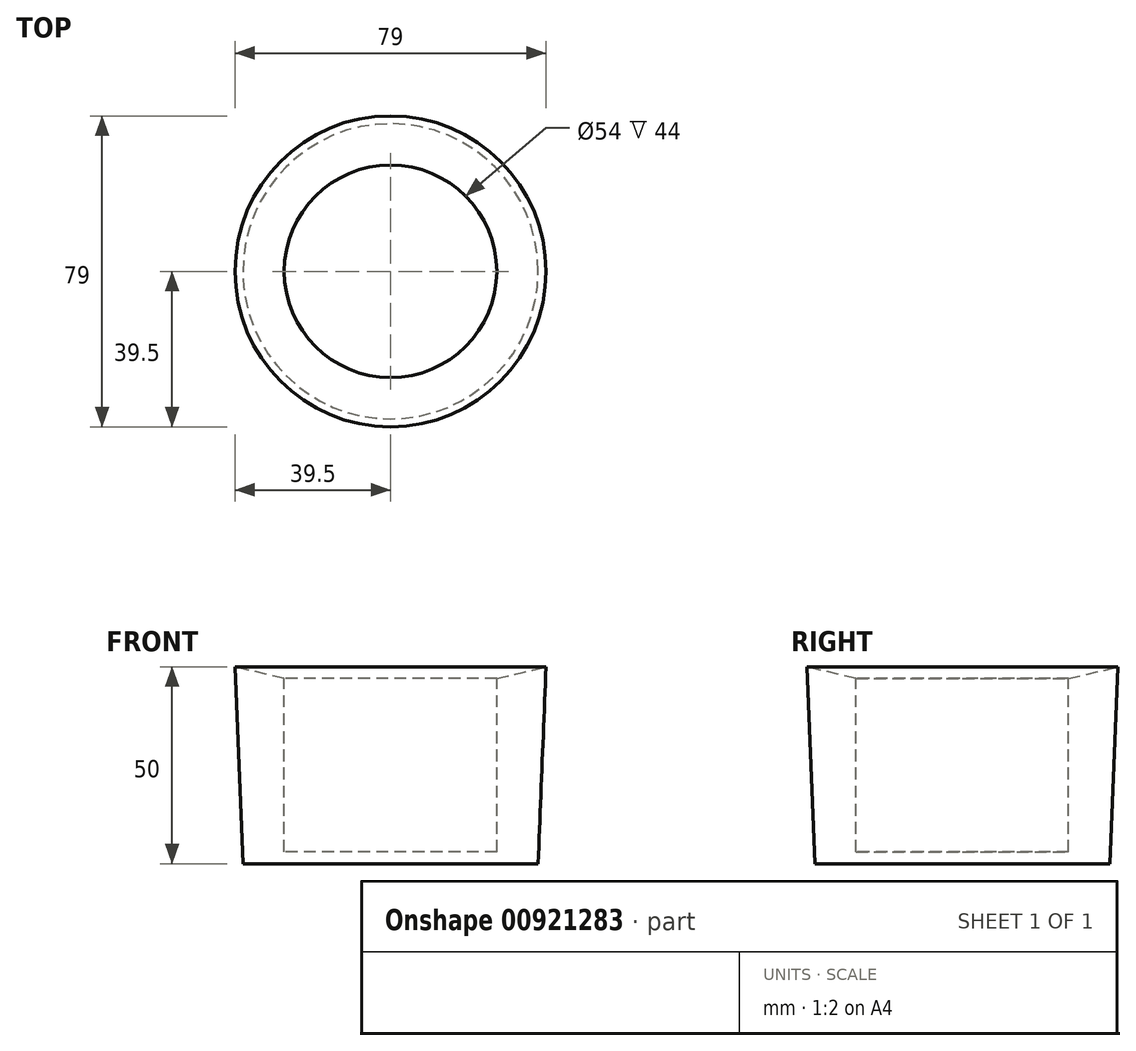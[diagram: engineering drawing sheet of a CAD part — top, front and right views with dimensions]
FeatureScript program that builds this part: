
annotation { "Feature Type Name" : "Feature", "Feature Type Description" : "" }
export const myFeature = defineFeature(function(context is Context, id is Id, definition is map)
    precondition{}
    {
        {
            var Q0;
            Q0=qCreatedBy(makeId("Front.planeOp"),FACE);
            var sketch = newSketch(context, id + "F0", { "sketchPlane" : qUnion([Q0])});
            skLineSegment(sketch, "E0", {"start": v(0, 0) * mm, "end": v(-37.5, 0) * mm});
            skLineSegment(sketch, "E1", {"start": v(-37.5, 0) * mm, "end": v(-39.5, 50) * mm});
            skLineSegment(sketch, "E2", {"start": v(-39.5, 50) * mm, "end": v(-27, 47) * mm});
            skLineSegment(sketch, "E3", {"start": v(-27, 47) * mm, "end": v(-27, 3) * mm});
            skLineSegment(sketch, "E4", {"start": v(-27, 3) * mm, "end": v(0, 3) * mm});
            skLineSegment(sketch, "E5", {"start": v(0, 3) * mm, "end": v(0, 0) * mm});
            skSolve(sketch);
        }
        {
            var Q0;
            Q0=makeQuery(id+"F0.imprint","IMPRINT",FACE,{"disambiguationData":[TD([[makeQuery(id+"F0.imprint","IMPRINT",EDGE,{"derivedFrom":sQuery(id+"F0.wireOp",EDGE,"E0")}),-1.0]])]});
            var Q1;
            Q1=sQuery(id+"F0.wireOp",EDGE,"E5");
            revolve(context, id + "F1", {"surfaceOperationType" : NewSurfaceOperationType.NEW, "entities" : qUnion([Q0]), "axis" : qUnion([Q1]), "revolveType" : RevolveType.FULL});
        }
    });
